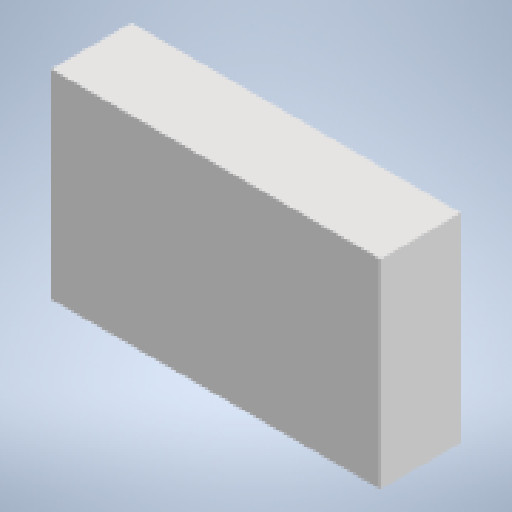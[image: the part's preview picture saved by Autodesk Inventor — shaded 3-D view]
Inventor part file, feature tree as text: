
AUTODESK INVENTOR PART (.ipt)
format: ipt  version: 2024.2 (Build 282272000, 272)  size: 175,616 bytes
history: native  units: mm
features: sketch x2, other x1, extrude x1
ambient origin geometry x8: Origin, YZ Plane, XZ Plane, XY Plane, X Axis, Y Axis, Z Axis, Center Point
bodies: Body1 (feature_tree)
feature tree (4):
  other  "Bryła1"
  extrude  "Wyciągnięcie proste1"  Depth=41.0mm
  sketch  "Szkic2"
  sketch  "Szkic1"
